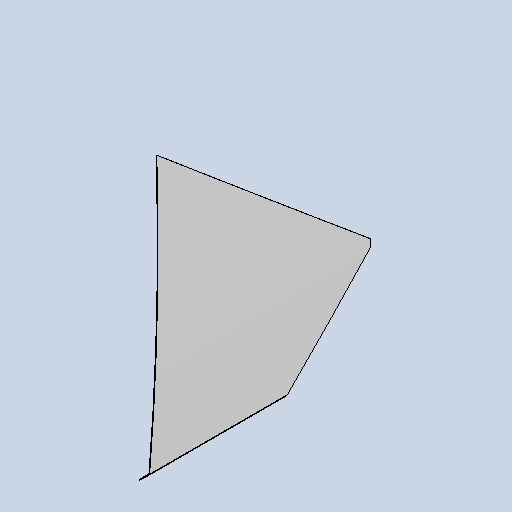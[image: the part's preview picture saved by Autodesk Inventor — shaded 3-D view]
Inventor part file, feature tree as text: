
AUTODESK INVENTOR PART (.ipt)
format: ipt  version: 2025 (Build 290162010, 162A)  size: 322,048 bytes
history: native  units: mm
features: other x4, sheet_metal_op x3, sketch x3, projected_geometry x3, extrude x1
ambient origin geometry x8: Origin, YZ Plane, XZ Plane, XY Plane, X Axis, Y Axis, Z Axis, Center Point
bodies: Body1 (feature_tree)
feature tree (14):
  sheet_metal_op  "Contour Flange2"
  extrude  "Extrusion3"  Depth=3.0mm
  other  "Mark5"
  other  "A-Side Definition"
  sketch  "Sketch1"  dims[d36=3.0mm d37=3.0mm]
  other  "Plate2"
  sheet_metal_op  "Bend2"
  sheet_metal_op  "Corner2"
  sketch  "Sketch5"  dims[d38=1.5mm]
  projected_geometry  "Projected Loop3"
  projected_geometry  "Projected Loop4"
  projected_geometry  "Projected Loop5"
  sketch  "Sketch8"  dims[d39=6.0mm d40=3.0mm d41=980.0mm d42=3.0mm d43=3.0mm d44=12.0mm d45=3.0mm d46=3.0mm d65=6.0mm d78=3.0mm d80=3.0mm d152=0.0mm d153=0.0mm d154=5.0mm d155=63.0mm d156=11050.0mm d157=23.736478mm d159=5.0mm d161=6.981317mm d162=6.981317mm d166=300.0mm d167=300.0mm d168=12.0mm d169=12.0mm d170=0.0mm d171=1843.0mm d172=566.0mm]
  other  "Definition1"
